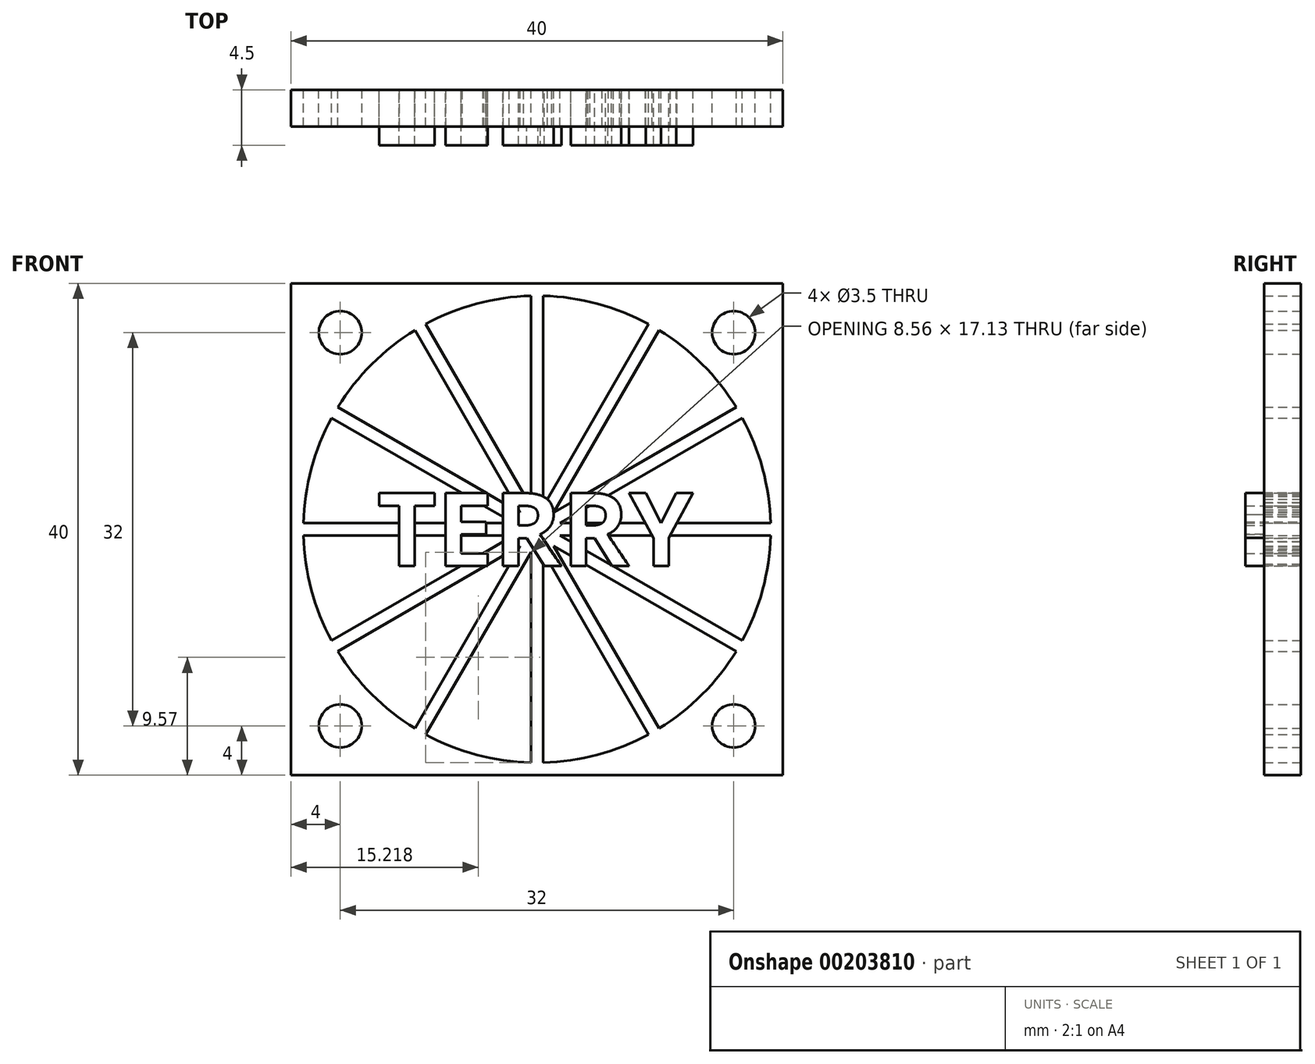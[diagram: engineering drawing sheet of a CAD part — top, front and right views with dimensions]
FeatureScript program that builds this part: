
annotation { "Feature Type Name" : "Feature", "Feature Type Description" : "" }
export const myFeature = defineFeature(function(context is Context, id is Id, definition is map)
    precondition{}
    {
        {
            var Q0;
            Q0=qCreatedBy(makeId("Front.planeOp"),FACE);
            var sketch = newSketch(context, id + "F0", { "sketchPlane" : qUnion([Q0])});
            skLineSegment(sketch, "E0.bottom", {"start": v(20, 20) * mm, "end": v(-20, 20) * mm});
            skLineSegment(sketch, "E0.top", {"start": v(20, -20) * mm, "end": v(-20, -20) * mm});
            skLineSegment(sketch, "E0.left", {"start": v(20, 20) * mm, "end": v(20, -20) * mm});
            skLineSegment(sketch, "E0.right", {"start": v(-20, 20) * mm, "end": v(-20, -20) * mm});
            skPoint(sketch, "E0.middle", {"position": v(0, 0) * mm});
            skArc(sketch, "E1", {"start": v(-0.5, 19) * mm, "mid": v(-4.92, 18.35) * mm, "end": v(-9.06, 16.7) * mm});
            skLineSegment(sketch, "E2", {"start": v(0, 0) * mm, "end": v(0, 16) * mm, "construction": true});
            skLineSegment(sketch, "E3", {"start": v(0, 16) * mm, "end": v(-16, 16) * mm, "construction": true});
            skCircle(sketch, "E4", {"center": v(-16, 16) * mm, "radius": 1.75 * mm});
            skCircle(sketch, "E5.MirrorC", {"center": v(16, 16) * mm, "radius": 1.75 * mm});
            skCircle(sketch, "E6.MirrorC", {"center": v(-16, -16) * mm, "radius": 1.75 * mm});
            skCircle(sketch, "E7.MirrorC", {"center": v(16, -16) * mm, "radius": 1.75 * mm});
            skLineSegment(sketch, "E8.0", {"start": v(-0.5, -19) * mm, "end": v(-0.5, -1.87) * mm});
            skLineSegment(sketch, "E9.MirrorCS", {"start": v(0.5, -19) * mm, "end": v(0.5, -1.87) * mm});
            skLineSegment(sketch, "E10.1.0", {"start": v(9.07, -16.7) * mm, "end": v(0.5, -1.87) * mm});
            skLineSegment(sketch, "E10.1.1", {"start": v(9.93, -16.2) * mm, "end": v(1.37, -1.37) * mm});
            skLineSegment(sketch, "E10.2.0", {"start": v(16.2, -9.93) * mm, "end": v(1.37, -1.37) * mm});
            skLineSegment(sketch, "E10.2.1", {"start": v(16.7, -9.07) * mm, "end": v(1.87, -0.5) * mm});
            skLineSegment(sketch, "E11.1.3.0", {"start": v(19, -0.5) * mm, "end": v(1.87, -0.5) * mm});
            skLineSegment(sketch, "E11.3.3.0", {"start": v(19, 0.5) * mm, "end": v(1.87, 0.5) * mm});
            skLineSegment(sketch, "E12.1.4.0", {"start": v(16.7, 9.07) * mm, "end": v(1.87, 0.5) * mm});
            skLineSegment(sketch, "E12.3.4.0", {"start": v(16.2, 9.93) * mm, "end": v(1.37, 1.37) * mm});
            skLineSegment(sketch, "E12.1.5.0", {"start": v(9.93, 16.2) * mm, "end": v(1.37, 1.37) * mm});
            skLineSegment(sketch, "E12.3.5.0", {"start": v(9.07, 16.7) * mm, "end": v(0.5, 1.87) * mm});
            skLineSegment(sketch, "E12.1.6.0", {"start": v(0.5, 19) * mm, "end": v(0.5, 1.87) * mm});
            skLineSegment(sketch, "E12.3.6.0", {"start": v(-0.5, 19) * mm, "end": v(-0.5, 1.87) * mm});
            skLineSegment(sketch, "E12.1.7.0", {"start": v(-9.07, 16.7) * mm, "end": v(-0.5, 1.87) * mm});
            skLineSegment(sketch, "E12.3.7.0", {"start": v(-9.93, 16.2) * mm, "end": v(-1.37, 1.37) * mm});
            skLineSegment(sketch, "E12.1.8.0", {"start": v(-16.2, 9.93) * mm, "end": v(-1.37, 1.37) * mm});
            skLineSegment(sketch, "E12.3.8.0", {"start": v(-16.7, 9.07) * mm, "end": v(-1.87, 0.5) * mm});
            skLineSegment(sketch, "E12.1.9.0", {"start": v(-19, 0.5) * mm, "end": v(-1.87, 0.5) * mm});
            skLineSegment(sketch, "E12.3.9.0", {"start": v(-19, -0.5) * mm, "end": v(-1.87, -0.5) * mm});
            skLineSegment(sketch, "E12.1.10.0", {"start": v(-16.7, -9.07) * mm, "end": v(-1.87, -0.5) * mm});
            skLineSegment(sketch, "E12.3.10.0", {"start": v(-16.2, -9.93) * mm, "end": v(-1.37, -1.37) * mm});
            skLineSegment(sketch, "E12.1.11.0", {"start": v(-9.93, -16.2) * mm, "end": v(-1.37, -1.37) * mm});
            skLineSegment(sketch, "E12.3.11.0", {"start": v(-9.07, -16.7) * mm, "end": v(-0.5, -1.87) * mm});
            skArc(sketch, "E13.trimOffspring", {"start": v(9.06, 16.7) * mm, "mid": v(4.92, 18.35) * mm, "end": v(0.5, 19) * mm});
            skArc(sketch, "E14.trimOffspring", {"start": v(16.2, 9.93) * mm, "mid": v(13.44, 13.44) * mm, "end": v(9.93, 16.2) * mm});
            skArc(sketch, "E15.trimOffspring", {"start": v(19, 0.5) * mm, "mid": v(18.35, 4.92) * mm, "end": v(16.7, 9.06) * mm});
            skArc(sketch, "E16.trimOffspring", {"start": v(16.7, -9.06) * mm, "mid": v(18.35, -4.92) * mm, "end": v(19, -0.5) * mm});
            skArc(sketch, "E17.trimOffspring", {"start": v(9.93, -16.2) * mm, "mid": v(13.44, -13.44) * mm, "end": v(16.2, -9.93) * mm});
            skArc(sketch, "E18.trimOffspring", {"start": v(0.5, -19) * mm, "mid": v(4.92, -18.35) * mm, "end": v(9.06, -16.7) * mm});
            skArc(sketch, "E19.trimOffspring", {"start": v(-9.06, -16.7) * mm, "mid": v(-4.92, -18.35) * mm, "end": v(-0.5, -19) * mm});
            skArc(sketch, "E20.trimOffspring", {"start": v(-16.2, -9.93) * mm, "mid": v(-13.44, -13.44) * mm, "end": v(-9.93, -16.2) * mm});
            skArc(sketch, "E21.trimOffspring", {"start": v(-16.7, 9.06) * mm, "mid": v(-18.35, 4.92) * mm, "end": v(-19, 0.5) * mm});
            skArc(sketch, "E22.trimOffspring", {"start": v(-9.93, 16.2) * mm, "mid": v(-13.44, 13.44) * mm, "end": v(-16.2, 9.93) * mm});
            skArc(sketch, "E23.trimOffspring", {"start": v(-19, -0.5) * mm, "mid": v(-18.35, -4.92) * mm, "end": v(-16.7, -9.06) * mm});
            skLineSegment(sketch, "E24.trimOffspring", {"start": v(-1.37, 1.37) * mm, "end": v(-16.2, 9.93) * mm});
            skLineSegment(sketch, "E25.trimOffspring", {"start": v(-1.37, 1.37) * mm, "end": v(-9.93, 16.2) * mm});
            skLineSegment(sketch, "E26.trimOffspring", {"start": v(-1.87, 0.5) * mm, "end": v(-19, 0.5) * mm});
            skLineSegment(sketch, "E27.trimOffspring", {"start": v(-1.87, 0.5) * mm, "end": v(-16.7, 9.07) * mm});
            skLineSegment(sketch, "E28.trimOffspring", {"start": v(-1.87, -0.5) * mm, "end": v(-16.7, -9.07) * mm});
            skLineSegment(sketch, "E29.trimOffspring", {"start": v(-1.87, -0.5) * mm, "end": v(-19, -0.5) * mm});
            skLineSegment(sketch, "E30.trimOffspring", {"start": v(-1.37, -1.37) * mm, "end": v(-9.93, -16.2) * mm});
            skLineSegment(sketch, "E31.trimOffspring", {"start": v(-1.37, -1.37) * mm, "end": v(-16.2, -9.93) * mm});
            skLineSegment(sketch, "E32.trimOffspring", {"start": v(-0.5, -1.87) * mm, "end": v(-0.5, -19) * mm});
            skLineSegment(sketch, "E33.trimOffspring", {"start": v(-0.5, -1.87) * mm, "end": v(-9.07, -16.7) * mm});
            skLineSegment(sketch, "E34.trimOffspring", {"start": v(0.5, -1.87) * mm, "end": v(9.07, -16.7) * mm});
            skLineSegment(sketch, "E35.trimOffspring", {"start": v(0.5, -1.87) * mm, "end": v(0.5, -19) * mm});
            skLineSegment(sketch, "E36.trimOffspring", {"start": v(1.37, -1.37) * mm, "end": v(16.2, -9.93) * mm});
            skLineSegment(sketch, "E37.trimOffspring", {"start": v(1.37, -1.37) * mm, "end": v(9.93, -16.2) * mm});
            skLineSegment(sketch, "E38.trimOffspring", {"start": v(1.87, -0.5) * mm, "end": v(19, -0.5) * mm});
            skLineSegment(sketch, "E39.trimOffspring", {"start": v(1.87, -0.5) * mm, "end": v(16.7, -9.07) * mm});
            skLineSegment(sketch, "E40.trimOffspring", {"start": v(1.87, 0.5) * mm, "end": v(16.7, 9.07) * mm});
            skLineSegment(sketch, "E41.trimOffspring", {"start": v(1.87, 0.5) * mm, "end": v(19, 0.5) * mm});
            skLineSegment(sketch, "E42.trimOffspring", {"start": v(1.37, 1.37) * mm, "end": v(9.93, 16.2) * mm});
            skLineSegment(sketch, "E43.trimOffspring", {"start": v(1.37, 1.37) * mm, "end": v(16.2, 9.93) * mm});
            skLineSegment(sketch, "E44.trimOffspring", {"start": v(0.5, 1.87) * mm, "end": v(0.5, 19) * mm});
            skLineSegment(sketch, "E45.trimOffspring", {"start": v(0.5, 1.87) * mm, "end": v(9.07, 16.7) * mm});
            skLineSegment(sketch, "E46.trimOffspring", {"start": v(-0.5, 1.87) * mm, "end": v(-9.07, 16.7) * mm});
            skLineSegment(sketch, "E47.trimOffspring", {"start": v(-0.5, 1.87) * mm, "end": v(-0.5, 19) * mm});
            skSolve(sketch);
        }
        {
            var Q0;
            Q0=makeQuery(id+"F0.imprint","IMPRINT",FACE,{"disambiguationData":[TD([[makeQuery(id+"F0.imprint","IMPRINT",EDGE,{"derivedFrom":sQuery(id+"F0.wireOp",EDGE,"E0.bottom")}),1.0]])]});
            extrude(context, id + "F1", {"entities" : qUnion([Q0]), "depth" : 3 * mm});
        }
        {
            var Q0;
            Q0=qCreatedBy(makeId("Front.planeOp"),FACE);
            var sketch = newSketch(context, id + "F2", { "sketchPlane" : qUnion([Q0])});
            skText(sketch, "E48", { "text": "TERRY", "fontName": "OpenSans-Bold.ttf"});
            const initialGuessF2  = {"E48": [-0.013, -0.003, 1, 0, 0.006]};
            skSetInitialGuess(sketch, initialGuessF2);
            skSolve(sketch);
        }
        {
            var Q0;
            Q0 = qSketchRegion(id + "F2", true);
            extrude(context, id + "F3", {"entities" : qUnion([Q0]), "operationType" : NewBodyOperationType.ADD, "depth" : 4.5 * mm});
        }
    });
